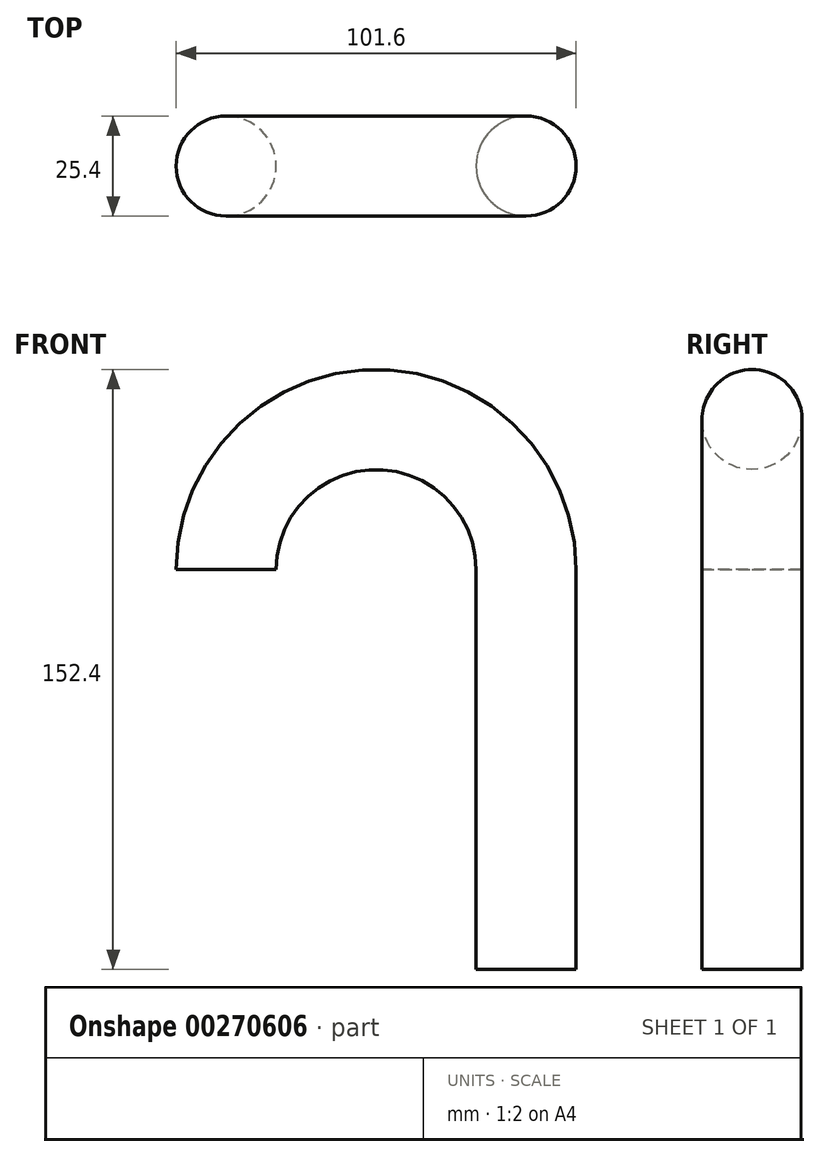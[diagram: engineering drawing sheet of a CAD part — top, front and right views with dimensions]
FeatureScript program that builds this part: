
annotation { "Feature Type Name" : "Feature", "Feature Type Description" : "" }
export const myFeature = defineFeature(function(context is Context, id is Id, definition is map)
    precondition{}
    {
        {
            var Q0;
            Q0=qCreatedBy(makeId("Top.planeOp"),FACE);
            var sketch = newSketch(context, id + "F0", { "sketchPlane" : qUnion([Q0])});
            skCircle(sketch, "E0", {"center": v(0, 0) * mm, "radius": 12.7 * mm});
            skSolve(sketch);
        }
        {
            var Q0;
            Q0=qCreatedBy(makeId("Front.planeOp"),FACE);
            var sketch = newSketch(context, id + "F1", { "sketchPlane" : qUnion([Q0])});
            skLineSegment(sketch, "E1", {"start": v(0, 0) * mm, "end": v(0, 101.6) * mm});
            skArc(sketch, "E2", {"start": v(0, 101.6) * mm, "mid": v(-38.1, 139.7) * mm, "end": v(-76.2, 101.6) * mm});
            skSolve(sketch);
        }
        {
            var Q0;
            Q0=makeQuery(id+"F0.imprint","IMPRINT",FACE,{"disambiguationData":[TD([[makeQuery(id+"F0.imprint","IMPRINT",EDGE,{"derivedFrom":sQuery(id+"F0.wireOp",EDGE,"E0")}),1.0]])]});
            var Q1;
            Q1=sQuery(id+"F1.wireOp",EDGE,"E2");
            var Q2;
            Q2=sQuery(id+"F1.wireOp",EDGE,"E1");
            sweep(context, id + "F2", {"profiles" : qUnion([Q0]), "path" : qUnion([Q1, Q2])});
        }
    });
